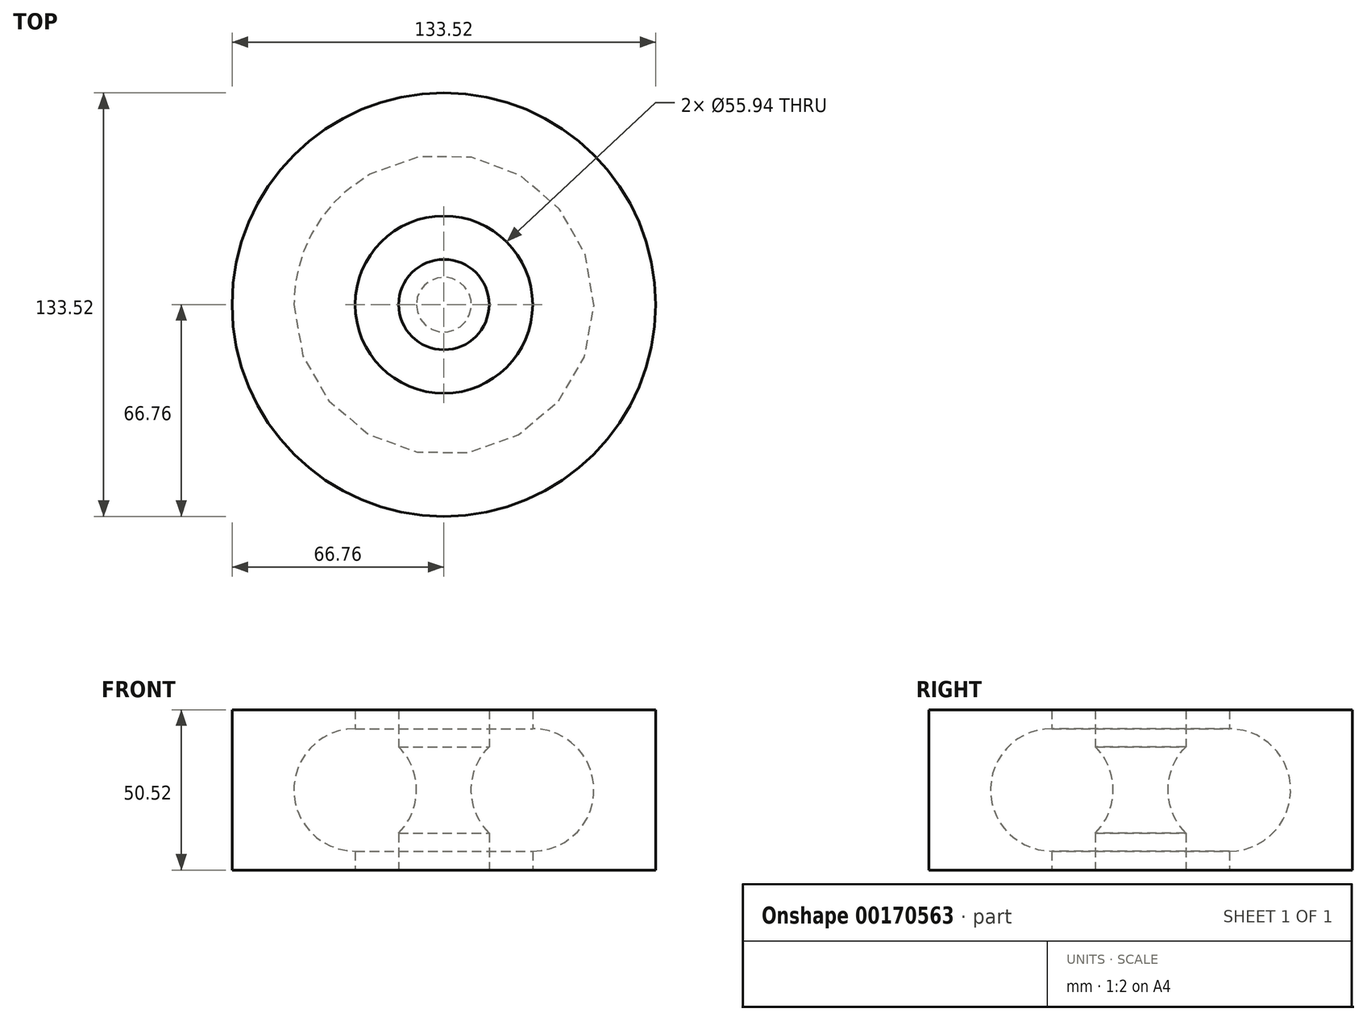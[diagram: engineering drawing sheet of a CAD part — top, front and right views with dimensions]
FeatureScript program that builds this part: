
annotation { "Feature Type Name" : "Feature", "Feature Type Description" : "" }
export const myFeature = defineFeature(function(context is Context, id is Id, definition is map)
    precondition{}
    {
        {
            var Q0;
            Q0=qCreatedBy(makeId("Front.planeOp"),FACE);
            var sketch = newSketch(context, id + "F0", { "sketchPlane" : qUnion([Q0])});
            skLineSegment(sketch, "E0", {"start": v(0, 0) * mm, "end": v(0, 50.52) * mm});
            skLineSegment(sketch, "E1", {"start": v(0, 50.52) * mm, "end": v(14.26, 50.52) * mm});
            skLineSegment(sketch, "E2", {"start": v(66.76, 50.52) * mm, "end": v(66.76, 0) * mm});
            skLineSegment(sketch, "E3", {"start": v(66.76, 0) * mm, "end": v(27.97, 0) * mm});
            skLineSegment(sketch, "E4", {"start": v(14.26, 0) * mm, "end": v(14.26, 11.65) * mm});
            skLineSegment(sketch, "E5", {"start": v(27.97, 0) * mm, "end": v(27.97, 5.94) * mm});
            skLineSegment(sketch, "E6.trimOffspring", {"start": v(27.97, 50.52) * mm, "end": v(66.76, 50.52) * mm});
            skLineSegment(sketch, "E7.trimOffspring", {"start": v(14.26, 0) * mm, "end": v(0, 0) * mm});
            skArc(sketch, "E8", {"start": v(14.26, 38.87) * mm, "mid": v(8.65, 25.26) * mm, "end": v(14.26, 11.65) * mm});
            skArc(sketch, "E9.trimOffspring", {"start": v(27.97, 5.94) * mm, "mid": v(47.29, 25.26) * mm, "end": v(27.97, 44.58) * mm});
            skLineSegment(sketch, "E10.trimOffspring", {"start": v(14.26, 38.87) * mm, "end": v(14.26, 50.52) * mm});
            skLineSegment(sketch, "E11.trimOffspring", {"start": v(27.97, 44.58) * mm, "end": v(27.97, 50.52) * mm});
            skSolve(sketch);
        }
        {
            var Q0;
            Q0 = qSketchRegion(id + "F0", true);
            var Q1;
            Q1=sQuery(id+"F0.wireOp",EDGE,"E0");
            revolve(context, id + "F1", {"entities" : qUnion([Q0]), "axis" : qUnion([Q1]), "revolveType" : RevolveType.FULL});
        }
    });
